# Revit family: Appliance_Cabinet-Danver-Grill_Base-Viking
name_source: partatom
category: Casework
units: mm (PartAtom-declared; Revit-internal decimal feet)

## family parameters
Always vertical = Yes
Classification Number = 23.40.35.17.47
Cut with Voids When Loaded = No
Room Calculation Point = No
Shared = No
Work Plane-Based = No

## types (1)
- Not a Type - Load Type Catalog
    C_Door1 = 0' - 6 31/32"
    C_Door2 = 1' - 9"
    C_Door3 = 2' - 11 1/32"
    C_Drawer1 = 0' - 5 3/32"
    C_Drawer2 = 1' - 3 5/32"
    C_DrawerA = 0' - 6 31/32"
    C_DrawerB = 1' - 9"
    C_DrawerC = 2' - 11 1/32"
    Cabinet Material = Metal - Danver - Stainless Steel
    Construction Type = 304 Grade Stainless Steel
    Default Elevation = 0' - 0"
    Depth = 2' - 0"
    Depth+Door = 2' - 0 7/8"
    Description = Please Load Accompanying Type Catalog (.txt)
    Door Count = 0
    Door Height = 1' - 8 1/8"
    Door Width = 1' - 1 29/32"
    Drawer Count = 6
    Drawer Height = 0' - 9 15/16"
    Drawer Width = 1' - 1 29/32"
    Grill Box Depth = 0' - 9 3/4"
    Grill Width = 3' - 0"
    Handle Material = Metal - Danver - Chrome Plated Steel
    Height = 2' - 6"
    Keynote = 12 35 28
    Manufacturer = Danver Outdoor Kitchens
    Manufacturer Note = Generic Grill shown, contact Danver for more information
    Model = Please Load Accompanying Type Catalog (.txt)
    Product Documentation Link = https://danver.com
    Product Name = Appliance Cabinet - Danver  - Viking Grill Base
    Product Page URL = https://danver.com
    Toe Height = 0' - 4 1/2"
    Toe Kick Material = Metal - Danver - Toe Kick
    URL = www.danver.com
    V_Door1 = No
    V_Door2 = No
    V_Door3 = No
    V_DrawerA1 = Yes
    V_DrawerA2 = Yes
    V_DrawerB1 = Yes
    V_DrawerB2 = Yes
    V_DrawerC1 = Yes
    V_DrawerC2 = Yes
    Version = 2019 - V1.0b
    Width = 3' - 6"

## geometry (parser evidence)
native form markers: Sweep x22
no freeform markers — native parametric forms only
